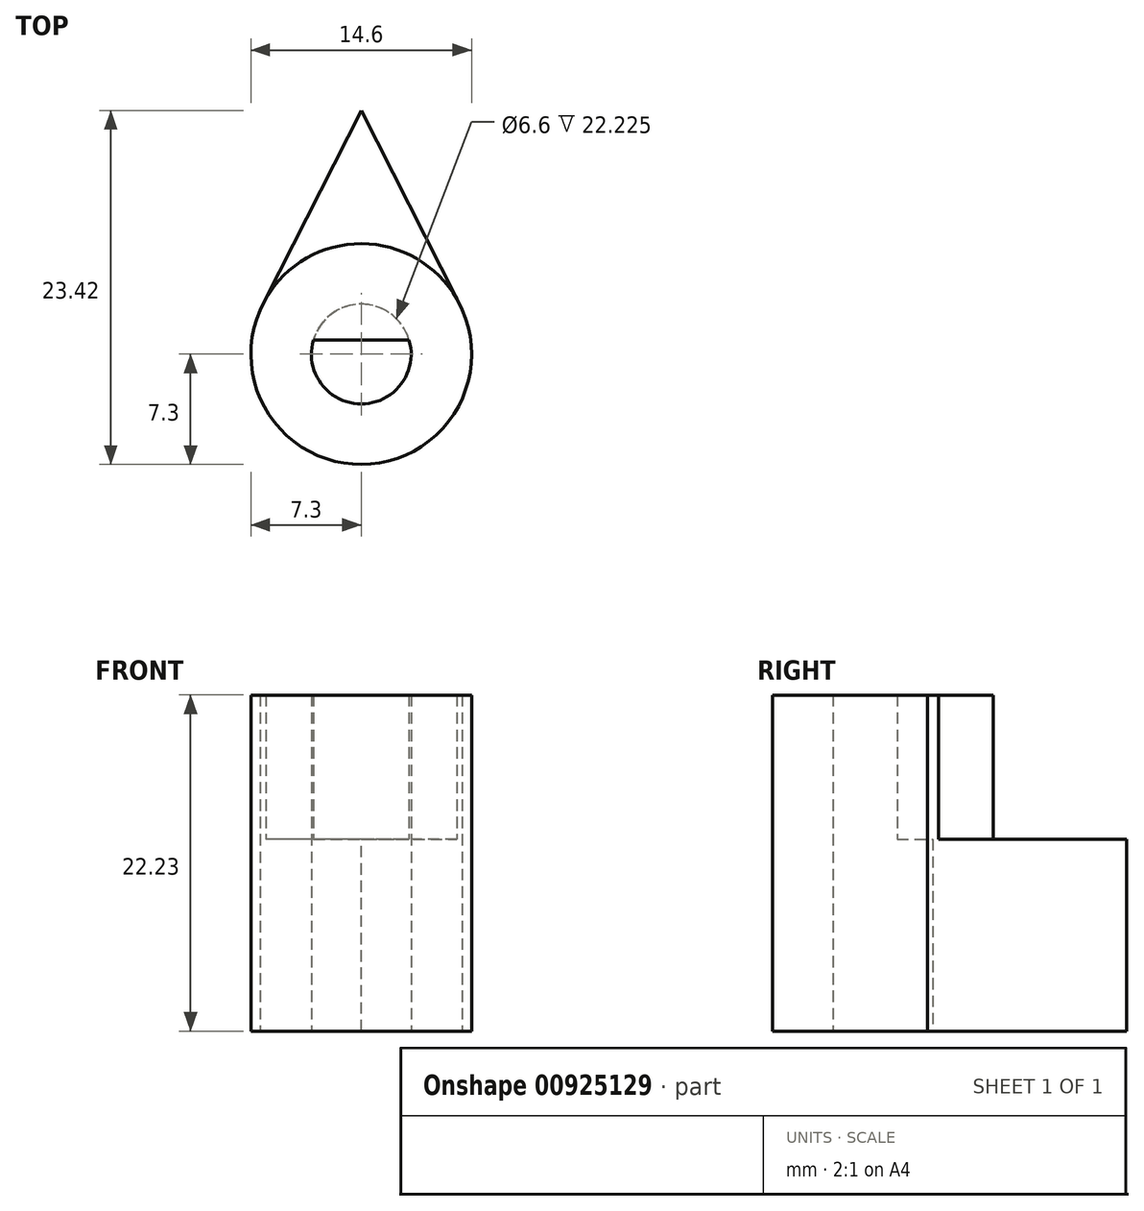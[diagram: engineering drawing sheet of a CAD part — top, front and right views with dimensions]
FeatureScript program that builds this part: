
annotation { "Feature Type Name" : "Feature", "Feature Type Description" : "" }
export const myFeature = defineFeature(function(context is Context, id is Id, definition is map)
    precondition{}
    {
        {
            var Q0;
            Q0=qCreatedBy(makeId("Top.planeOp"),FACE);
            var sketch = newSketch(context, id + "F0", { "sketchPlane" : qUnion([Q0])});
            skCircle(sketch, "E0", {"center": v(0, 0) * mm, "radius": 3.3 * mm});
            skCircle(sketch, "E1", {"center": v(0, 0) * mm, "radius": 7.3 * mm});
            skPoint(sketch, "E2", {"position": v(0, -3.3) * mm});
            skLineSegment(sketch, "E3", {"start": v(0, 16.12) * mm, "end": v(-6.7, 2.9) * mm});
            skLineSegment(sketch, "E4", {"start": v(0, 16.12) * mm, "end": v(6.69, 2.93) * mm});
            skLineSegment(sketch, "E5", {"start": v(-3.17, 0.94) * mm, "end": v(3.17, 0.94) * mm});
            skSolve(sketch);
        }
        {
            var Q0;
            {var subQ5=sQuery(id+"F0.wireOp",EDGE,"9UYlJdJK-QgIJ-yJPl-AHFd-2qOA43bLn9To");var subQ6=sQuery(id+"F0.wireOp",EDGE,"E0");var subQ7=makeQuery(id+"F0.imprint","INTERSECT",VERTEX,{"disambiguationData":[OD(0.0)],"derivedFrom":[subQ6,subQ5]});Q0=makeQuery(id+"F0.imprint","IMPRINT",FACE,{"disambiguationData":[TD([[makeQuery(id+"F0.imprint","IMPRINT",EDGE,{"disambiguationData":[TD([[subQ7,1.0]])],"derivedFrom":subQ6}),-1.0]])]});}
            var Q1;
            {var subQ0=sQuery(id+"F0.wireOp",EDGE,"9UYlJdJK-QgIJ-yJPl-AHFd-2qOA43bLn9To");Q1=makeQuery(id+"F0.imprint","IMPRINT",FACE,{"disambiguationData":[TD([[makeQuery(id+"F0.imprint","IMPRINT",EDGE,{"derivedFrom":subQ0}),1.0]])]});}
            extrude(context, id + "F1", {"entities" : qUnion([Q0, Q1]), "depth" : 9.52 * mm, "offsetDistance" : 25.4 * mm});
        }
        {
            var Q0;
            {var subQ0=sQuery(id+"F0.wireOp",EDGE,"9UYlJdJK-QgIJ-yJPl-AHFd-2qOA43bLn9To");Q0=makeQuery(id+"F0.imprint","IMPRINT",FACE,{"disambiguationData":[TD([[makeQuery(id+"F0.imprint","IMPRINT",EDGE,{"derivedFrom":subQ0}),1.0]])]});}
            var Q1;
            {var subQ0=sQuery(id+"F0.wireOp",EDGE,"9UYlJdJK-QgIJ-yJPl-AHFd-2qOA43bLn9To");Q1=makeQuery(id+"F0.imprint","IMPRINT",FACE,{"disambiguationData":[TD([[makeQuery(id+"F0.imprint","IMPRINT",EDGE,{"derivedFrom":subQ0}),-1.0]])]});}
            var Q2;
            {var subQ0=sQuery(id+"F0.wireOp",EDGE,"E4");var subQ1=sQuery(id+"F0.wireOp",EDGE,"E1");var subQ2=makeQuery(id+"F0.imprint","INTERSECT",VERTEX,{"disambiguationData":[OD(1.0)],"derivedFrom":[subQ1,subQ0]});Q2=makeQuery(id+"F0.imprint","IMPRINT",FACE,{"disambiguationData":[TD([[makeQuery(id+"F0.imprint","IMPRINT",EDGE,{"disambiguationData":[TD([[subQ2,-1.0]])],"derivedFrom":subQ1}),-1.0]])]});}
            var Q3;
            {var subQ5=sQuery(id+"F0.wireOp",EDGE,"9UYlJdJK-QgIJ-yJPl-AHFd-2qOA43bLn9To");var subQ6=sQuery(id+"F0.wireOp",EDGE,"E0");var subQ7=makeQuery(id+"F0.imprint","INTERSECT",VERTEX,{"disambiguationData":[OD(0.0)],"derivedFrom":[subQ6,subQ5]});Q3=makeQuery(id+"F0.imprint","IMPRINT",FACE,{"disambiguationData":[TD([[makeQuery(id+"F0.imprint","IMPRINT",EDGE,{"disambiguationData":[TD([[subQ7,1.0]])],"derivedFrom":subQ6}),-1.0]])]});}
            extrude(context, id + "F2", {"entities" : qUnion([Q0, Q1, Q2, Q3]), "depth" : -12.7 * mm, "offsetDistance" : 25.4 * mm});
        }
        {
            var Q0;
            {var subQ0=sQuery(id+"F0.wireOp",EDGE,"E5");Q0=makeQuery(id+"F0.imprint","IMPRINT",FACE,{"disambiguationData":[TD([[makeQuery(id+"F0.imprint","IMPRINT",EDGE,{"derivedFrom":subQ0}),1.0]])]});}
            var Q1;
            Q1=makeQuery(id+"F1.opExtrude","CAP_FACE",FACE,{"disambiguationData":[OSD([sQuery(id+"F0.wireOp",EDGE,"E0"),sQuery(id+"F0.wireOp",EDGE,"E1"),sQuery(id+"F0.wireOp",EDGE,"E3"),sQuery(id+"F0.wireOp",EDGE,"E4")])],"isStart":false});
            extrude(context, id + "F3", {"entities" : qUnion([Q0]), "operationType" : NewBodyOperationType.ADD, "endBound" : BoundingType.UP_TO_SURFACE, "depth" : 9.9 * mm, "endBoundEntityFace" : qUnion([Q1]), "offsetDistance" : 25.4 * mm});
        }
        {
            var Q0;
            Q0=sQuery(id+"F0.wireOp",EDGE,"E0");
            extrude(context, id + "F4", {"bodyType" : ToolBodyType.SURFACE, "surfaceEntities" : qUnion([Q0]), "depth" : 12.7 * mm, "offsetDistance" : 25.4 * mm});
        }
    });
